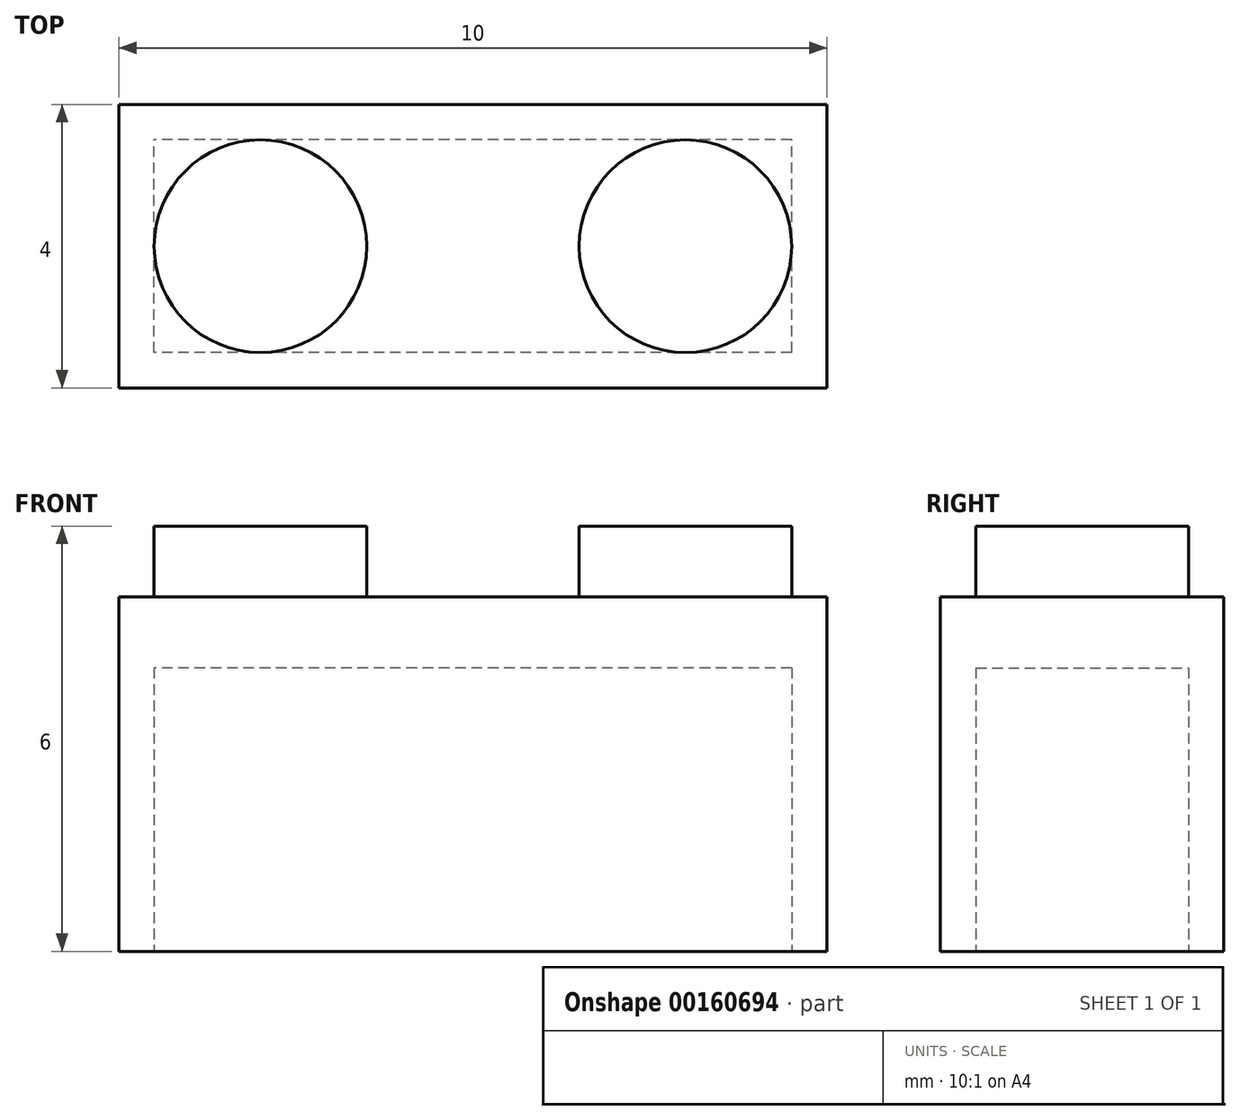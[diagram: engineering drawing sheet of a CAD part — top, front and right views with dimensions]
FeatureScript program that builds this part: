
annotation { "Feature Type Name" : "Feature", "Feature Type Description" : "" }
export const myFeature = defineFeature(function(context is Context, id is Id, definition is map)
    precondition{}
    {
        {
            var Q0;
            Q0=qCreatedBy(makeId("Top.planeOp"),FACE);
            var sketch = newSketch(context, id + "F0", { "sketchPlane" : qUnion([Q0])});
            skLineSegment(sketch, "E0.bottom", {"start": v(5, 2) * mm, "end": v(-5, 2) * mm});
            skLineSegment(sketch, "E0.top", {"start": v(5, -2) * mm, "end": v(-5, -2) * mm});
            skLineSegment(sketch, "E0.left", {"start": v(5, 2) * mm, "end": v(5, -2) * mm});
            skLineSegment(sketch, "E0.right", {"start": v(-5, 2) * mm, "end": v(-5, -2) * mm});
            skPoint(sketch, "E0.middle", {"position": v(0, 0) * mm});
            skSolve(sketch);
        }
        {
            var Q0;
            Q0 = qSketchRegion(id + "F0", true);
            extrude(context, id + "F1", {"entities" : qUnion([Q0]), "depth" : 5 * mm});
        }
        {
            var Q0;
            Q0=makeQuery(id+"F1.opExtrude","CAP_FACE",FACE,{"disambiguationData":[OSD([sQuery(id+"F0.wireOp",EDGE,"E0.bottom"),sQuery(id+"F0.wireOp",EDGE,"E0.top"),sQuery(id+"F0.wireOp",EDGE,"E0.left"),sQuery(id+"F0.wireOp",EDGE,"E0.right")])],"isStart":true});
            var sketch = newSketch(context, id + "F2", { "sketchPlane" : qUnion([Q0])});
            skLineSegment(sketch, "E1.bottom", {"start": v(4.5, 1.5) * mm, "end": v(-4.5, 1.5) * mm});
            skLineSegment(sketch, "E1.top", {"start": v(4.5, -1.5) * mm, "end": v(-4.5, -1.5) * mm});
            skLineSegment(sketch, "E1.left", {"start": v(4.5, 1.5) * mm, "end": v(4.5, -1.5) * mm});
            skLineSegment(sketch, "E1.right", {"start": v(-4.5, 1.5) * mm, "end": v(-4.5, -1.5) * mm});
            skPoint(sketch, "E1.middle", {"position": v(0, 0) * mm});
            skSolve(sketch);
        }
        {
            var Q0;
            Q0 = qSketchRegion(id + "F2", true);
            extrude(context, id + "F3", {"entities" : qUnion([Q0]), "operationType" : NewBodyOperationType.REMOVE, "oppositeDirection" : true, "depth" : 4 * mm});
        }
        {
            var Q0;
            Q0=makeQuery(id+"F1.opExtrude","CAP_FACE",FACE,{"disambiguationData":[OSD([sQuery(id+"F0.wireOp",EDGE,"E0.bottom"),sQuery(id+"F0.wireOp",EDGE,"E0.top"),sQuery(id+"F0.wireOp",EDGE,"E0.left"),sQuery(id+"F0.wireOp",EDGE,"E0.right")])],"isStart":false});
            var sketch = newSketch(context, id + "F4", { "sketchPlane" : qUnion([Q0])});
            skCircle(sketch, "E2", {"center": v(-3, 0) * mm, "radius": 1.5 * mm});
            skCircle(sketch, "E3", {"center": v(3, 0) * mm, "radius": 1.5 * mm});
            skSolve(sketch);
        }
        {
            var Q0;
            Q0 = qSketchRegion(id + "F4", true);
            extrude(context, id + "F5", {"entities" : qUnion([Q0]), "operationType" : NewBodyOperationType.ADD, "depth" : 1 * mm});
        }
    });
